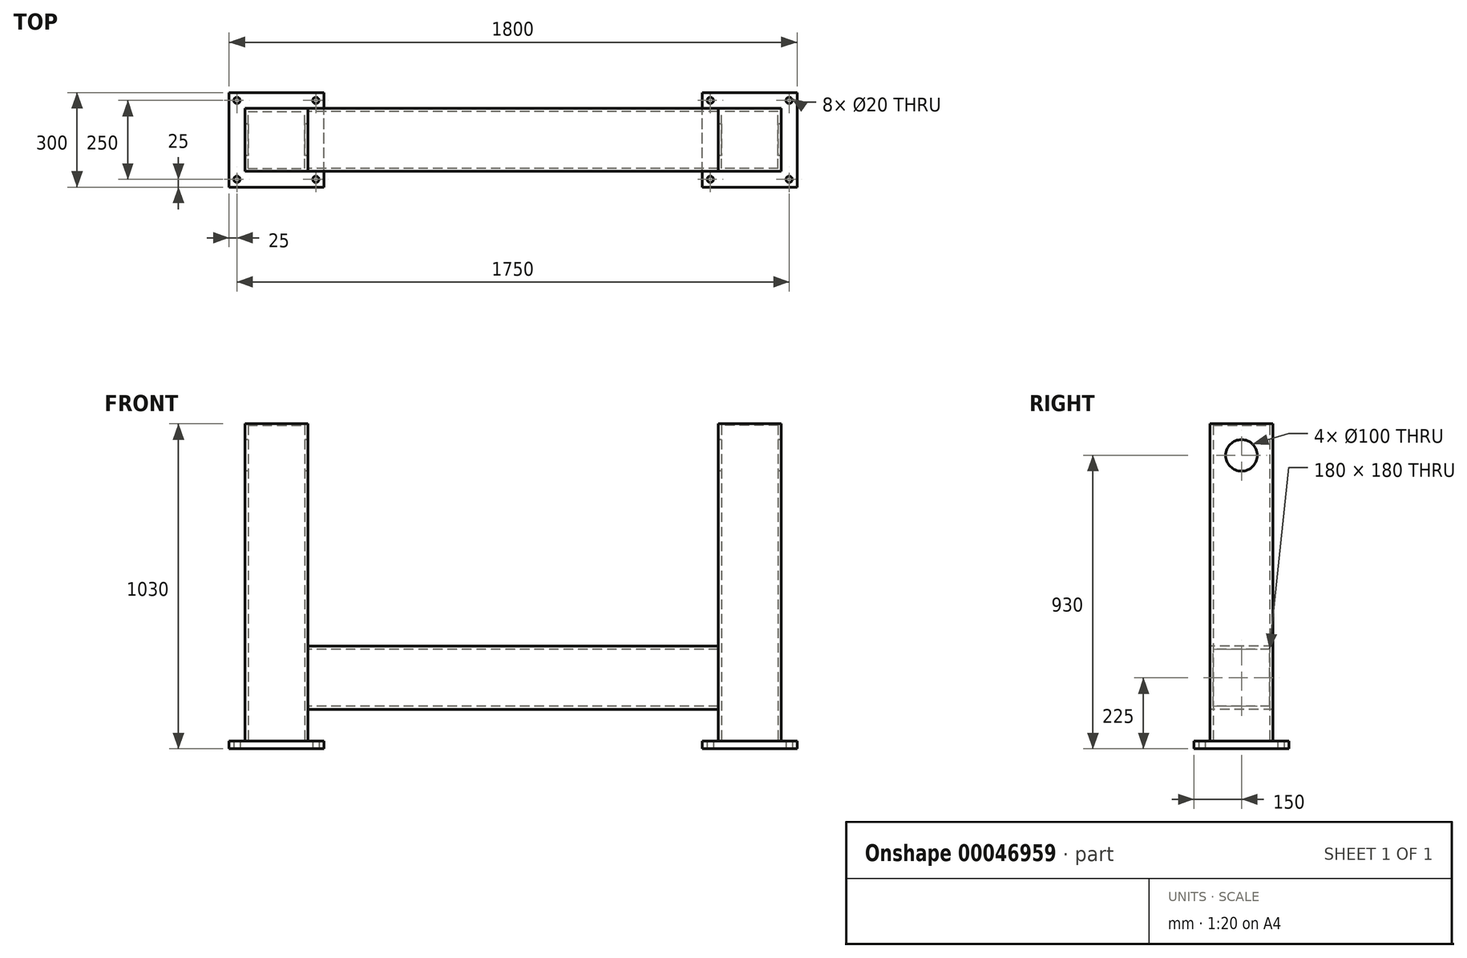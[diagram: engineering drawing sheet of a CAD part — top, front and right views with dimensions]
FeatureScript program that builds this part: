
annotation { "Feature Type Name" : "Feature", "Feature Type Description" : "" }
export const myFeature = defineFeature(function(context is Context, id is Id, definition is map)
    precondition{}
    {
        {
            var Q0;
            Q0=qCreatedBy(makeId("Top.planeOp"),FACE);
            var sketch = newSketch(context, id + "F0", { "sketchPlane" : qUnion([Q0])});
            skLineSegment(sketch, "E0.bottom", {"start": v(-900, -150) * mm, "end": v(-600, -150) * mm});
            skLineSegment(sketch, "E0.top", {"start": v(-900, 150) * mm, "end": v(-600, 150) * mm});
            skLineSegment(sketch, "E0.left", {"start": v(-900, -150) * mm, "end": v(-900, 150) * mm});
            skLineSegment(sketch, "E0.right", {"start": v(-600, -150) * mm, "end": v(-600, 150) * mm});
            skPoint(sketch, "E0.middle", {"position": v(-750, 0) * mm});
            skLineSegment(sketch, "E1.bottom", {"start": v(-875, 125) * mm, "end": v(-625, 125) * mm, "construction": true});
            skLineSegment(sketch, "E1.top", {"start": v(-875, -125) * mm, "end": v(-625, -125) * mm, "construction": true});
            skLineSegment(sketch, "E1.left", {"start": v(-875, 125) * mm, "end": v(-875, -125) * mm, "construction": true});
            skLineSegment(sketch, "E1.right", {"start": v(-625, 125) * mm, "end": v(-625, -125) * mm, "construction": true});
            skCircle(sketch, "E2", {"center": v(-625, 125) * mm, "radius": 10 * mm});
            skCircle(sketch, "E3", {"center": v(-875, 125) * mm, "radius": 10 * mm});
            skCircle(sketch, "E4", {"center": v(-875, -125) * mm, "radius": 10 * mm});
            skCircle(sketch, "E5", {"center": v(-625, -125) * mm, "radius": 10 * mm});
            skCircle(sketch, "E6.MirrorC", {"center": v(625, -125) * mm, "radius": 10 * mm});
            skCircle(sketch, "E7.MirrorC", {"center": v(875, -125) * mm, "radius": 10 * mm});
            skCircle(sketch, "E8.MirrorC", {"center": v(875, 125) * mm, "radius": 10 * mm});
            skCircle(sketch, "E9.MirrorC", {"center": v(625, 125) * mm, "radius": 10 * mm});
            skLineSegment(sketch, "E10.MirrorCS", {"start": v(900, -150) * mm, "end": v(600, -150) * mm});
            skPoint(sketch, "E11.MirrorP", {"position": v(750, 0) * mm});
            skLineSegment(sketch, "E12.MirrorCS", {"start": v(875, -125) * mm, "end": v(625, -125) * mm, "construction": true});
            skLineSegment(sketch, "E13.MirrorCS", {"start": v(900, 150) * mm, "end": v(600, 150) * mm});
            skLineSegment(sketch, "E14.MirrorCS", {"start": v(900, -150) * mm, "end": v(900, 150) * mm});
            skLineSegment(sketch, "E15.MirrorCS", {"start": v(600, -150) * mm, "end": v(600, 150) * mm});
            skLineSegment(sketch, "E16.MirrorCS", {"start": v(875, 125) * mm, "end": v(625, 125) * mm, "construction": true});
            skLineSegment(sketch, "E17.MirrorCS", {"start": v(875, 125) * mm, "end": v(875, -125) * mm, "construction": true});
            skLineSegment(sketch, "E18.MirrorCS", {"start": v(625, 125) * mm, "end": v(625, -125) * mm, "construction": true});
            skSolve(sketch);
        }
        {
            var Q0;
            Q0 = qSketchRegion(id + "F0", true);
            extrude(context, id + "F1", {"entities" : qUnion([Q0]), "depth" : 25 * mm});
        }
        {
            var Q0;
            Q0=makeQuery(id+"F1.opExtrude","CAP_FACE",FACE,{"disambiguationData":[OSD([sQuery(id+"F0.wireOp",EDGE,"E0.bottom"),sQuery(id+"F0.wireOp",EDGE,"E0.top"),sQuery(id+"F0.wireOp",EDGE,"E0.left"),sQuery(id+"F0.wireOp",EDGE,"E0.right"),sQuery(id+"F0.wireOp",EDGE,"E2"),sQuery(id+"F0.wireOp",EDGE,"E3"),sQuery(id+"F0.wireOp",EDGE,"E4"),sQuery(id+"F0.wireOp",EDGE,"E5")])],"isStart":false});
            var sketch = newSketch(context, id + "F2", { "sketchPlane" : qUnion([Q0])});
            skLineSegment(sketch, "E19.bottom", {"start": v(-850, -100) * mm, "end": v(-650, -100) * mm});
            skLineSegment(sketch, "E19.top", {"start": v(-850, 100) * mm, "end": v(-650, 100) * mm});
            skLineSegment(sketch, "E19.left", {"start": v(-850, -100) * mm, "end": v(-850, 100) * mm});
            skLineSegment(sketch, "E19.right", {"start": v(-650, -100) * mm, "end": v(-650, 100) * mm});
            skPoint(sketch, "E19.middle", {"position": v(-750, 0) * mm});
            skPoint(sketch, "E19.middle.positionSnap0", {"position": v(-750, -150) * mm});
            skPoint(sketch, "E19.centerSnap0", {"position": v(-750, -150) * mm});
            skLineSegment(sketch, "E20.bottom", {"start": v(-840, -90) * mm, "end": v(-660, -90) * mm});
            skLineSegment(sketch, "E20.top", {"start": v(-840, 90) * mm, "end": v(-660, 90) * mm});
            skLineSegment(sketch, "E20.left", {"start": v(-840, -90) * mm, "end": v(-840, 90) * mm});
            skLineSegment(sketch, "E20.right", {"start": v(-660, -90) * mm, "end": v(-660, 90) * mm});
            skPoint(sketch, "E21.MirrorP", {"position": v(750, -150) * mm});
            skPoint(sketch, "E22.MirrorP", {"position": v(750, 0) * mm});
            skLineSegment(sketch, "E23.MirrorCS", {"start": v(850, -100) * mm, "end": v(650, -100) * mm});
            skLineSegment(sketch, "E24.MirrorCS", {"start": v(850, 100) * mm, "end": v(650, 100) * mm});
            skLineSegment(sketch, "E25.MirrorCS", {"start": v(850, -100) * mm, "end": v(850, 100) * mm});
            skLineSegment(sketch, "E26.MirrorCS", {"start": v(650, -100) * mm, "end": v(650, 100) * mm});
            skLineSegment(sketch, "E27.MirrorCS", {"start": v(840, -90) * mm, "end": v(660, -90) * mm});
            skLineSegment(sketch, "E28.MirrorCS", {"start": v(660, -90) * mm, "end": v(660, 90) * mm});
            skLineSegment(sketch, "E29.MirrorCS", {"start": v(840, -90) * mm, "end": v(840, 90) * mm});
            skLineSegment(sketch, "E30.MirrorCS", {"start": v(840, 90) * mm, "end": v(660, 90) * mm});
            skSolve(sketch);
        }
        {
            var Q0;
            Q0 = qSketchRegion(id + "F2", true);
            extrude(context, id + "F3", {"entities" : qUnion([Q0]), "depth" : 1000 * mm});
        }
        {
            var Q0;
            Q0=makeQuery(id+"F3.opExtrude","SWEPT_FACE",FACE,{"disambiguationData":[OSD([sQuery(id+"F2.wireOp",EDGE,"E19.right")])]});
            var sketch = newSketch(context, id + "F4", { "sketchPlane" : qUnion([Q0])});
            skLineSegment(sketch, "E31.bottom", {"start": v(-100, 325) * mm, "end": v(100, 325) * mm});
            skLineSegment(sketch, "E31.top", {"start": v(-100, 125) * mm, "end": v(100, 125) * mm});
            skLineSegment(sketch, "E31.left", {"start": v(-100, 325) * mm, "end": v(-100, 125) * mm});
            skLineSegment(sketch, "E31.right", {"start": v(100, 325) * mm, "end": v(100, 125) * mm});
            skLineSegment(sketch, "E32.bottom", {"start": v(-90, 315) * mm, "end": v(90, 315) * mm});
            skLineSegment(sketch, "E32.top", {"start": v(-90, 135) * mm, "end": v(90, 135) * mm});
            skLineSegment(sketch, "E32.left", {"start": v(-90, 315) * mm, "end": v(-90, 135) * mm});
            skLineSegment(sketch, "E32.right", {"start": v(90, 315) * mm, "end": v(90, 135) * mm});
            skSolve(sketch);
        }
        {
            var Q0;
            Q0 = qSketchRegion(id + "F4", true);
            var Q1;
            Q1=makeQuery(id+"F4.imprint","IMPRINT",FACE,{"disambiguationData":[TD([[makeQuery(id+"F4.imprint","IMPRINT",EDGE,{"derivedFrom":sQuery(id+"F4.wireOp",EDGE,"E31.bottom")}),-1.0]])]});
            var Q2;
            Q2=makeQuery(id+"F3.opExtrude","SWEPT_BODY",BODY,{"disambiguationData":[OSD([sQuery(id+"F2.wireOp",EDGE,"E23.MirrorCS"),sQuery(id+"F2.wireOp",EDGE,"E24.MirrorCS"),sQuery(id+"F2.wireOp",EDGE,"E25.MirrorCS"),sQuery(id+"F2.wireOp",EDGE,"E26.MirrorCS"),sQuery(id+"F2.wireOp",EDGE,"E27.MirrorCS"),sQuery(id+"F2.wireOp",EDGE,"E28.MirrorCS"),sQuery(id+"F2.wireOp",EDGE,"E29.MirrorCS"),sQuery(id+"F2.wireOp",EDGE,"E30.MirrorCS")])]});
            extrude(context, id + "F5", {"entities" : qUnion([Q0, Q1]), "endBound" : BoundingType.UP_TO_BODY, "endBoundEntityBody" : qUnion([Q2]), "depth" : 25 * mm});
        }
        {
            var Q0;
            Q0=makeQuery(id+"F3.opExtrude","CAP_FACE",FACE,{"disambiguationData":[OSD([sQuery(id+"F2.wireOp",EDGE,"E19.bottom"),sQuery(id+"F2.wireOp",EDGE,"E19.top"),sQuery(id+"F2.wireOp",EDGE,"E19.left"),sQuery(id+"F2.wireOp",EDGE,"E19.right"),sQuery(id+"F2.wireOp",EDGE,"E20.bottom"),sQuery(id+"F2.wireOp",EDGE,"E20.top"),sQuery(id+"F2.wireOp",EDGE,"E20.left"),sQuery(id+"F2.wireOp",EDGE,"E20.right")])],"isStart":false});
            var sketch = newSketch(context, id + "F6", { "sketchPlane" : qUnion([Q0])});
            skLineSegment(sketch, "E33.bottom", {"start": v(-850, 100) * mm, "end": v(-650, 100) * mm});
            skLineSegment(sketch, "E33.top", {"start": v(-850, -100) * mm, "end": v(-650, -100) * mm});
            skLineSegment(sketch, "E33.left", {"start": v(-850, 100) * mm, "end": v(-850, -100) * mm});
            skLineSegment(sketch, "E33.right", {"start": v(-650, 100) * mm, "end": v(-650, -100) * mm});
            skSolve(sketch);
        }
        {
            var Q0;
            Q0 = qSketchRegion(id + "F6", true);
            extrude(context, id + "F7", {"entities" : qUnion([Q0]), "operationType" : NewBodyOperationType.ADD, "depth" : 5 * mm});
        }
        {
            var Q0;
            Q0=makeQuery(id+"F3.opExtrude","CAP_FACE",FACE,{"disambiguationData":[OSD([sQuery(id+"F2.wireOp",EDGE,"E23.MirrorCS"),sQuery(id+"F2.wireOp",EDGE,"E24.MirrorCS"),sQuery(id+"F2.wireOp",EDGE,"E25.MirrorCS"),sQuery(id+"F2.wireOp",EDGE,"E26.MirrorCS"),sQuery(id+"F2.wireOp",EDGE,"E27.MirrorCS"),sQuery(id+"F2.wireOp",EDGE,"E28.MirrorCS"),sQuery(id+"F2.wireOp",EDGE,"E29.MirrorCS"),sQuery(id+"F2.wireOp",EDGE,"E30.MirrorCS")])],"isStart":false});
            var sketch = newSketch(context, id + "F8", { "sketchPlane" : qUnion([Q0])});
            skLineSegment(sketch, "E34.bottom", {"start": v(650, 100) * mm, "end": v(850, 100) * mm});
            skLineSegment(sketch, "E34.top", {"start": v(650, -100) * mm, "end": v(850, -100) * mm});
            skLineSegment(sketch, "E34.left", {"start": v(650, 100) * mm, "end": v(650, -100) * mm});
            skLineSegment(sketch, "E34.right", {"start": v(850, 100) * mm, "end": v(850, -100) * mm});
            skSolve(sketch);
        }
        {
            var Q0;
            Q0 = qSketchRegion(id + "F8", true);
            extrude(context, id + "F9", {"entities" : qUnion([Q0]), "operationType" : NewBodyOperationType.ADD, "depth" : 5 * mm});
        }
        {
            var Q0;
            Q0=makeQuery(id+"F7.boolean.opBoolean","MERGE",FACE,{"derivedFrom":[makeQuery(id+"F3.opExtrude","SWEPT_FACE",FACE,{"disambiguationData":[OSD([sQuery(id+"F2.wireOp",EDGE,"E19.left")])]}),makeQuery(id+"F7.opExtrude","SWEPT_FACE",FACE,{"disambiguationData":[OSD([sQuery(id+"F6.wireOp",EDGE,"E33.left")])]})]});
            var sketch = newSketch(context, id + "F10", { "sketchPlane" : qUnion([Q0])});
            skLineSegment(sketch, "E35", {"start": v(0, 1030) * mm, "end": v(0, 930) * mm, "construction": true});
            skCircle(sketch, "E36", {"center": v(0, 930) * mm, "radius": 50 * mm});
            skSolve(sketch);
        }
        {
            var Q0;
            Q0 = qSketchRegion(id + "F10", true);
            extrude(context, id + "F11", {"entities" : qUnion([Q0]), "operationType" : NewBodyOperationType.REMOVE, "endBound" : BoundingType.THROUGH_ALL, "oppositeDirection" : true, "depth" : 25 * mm});
        }
    });
